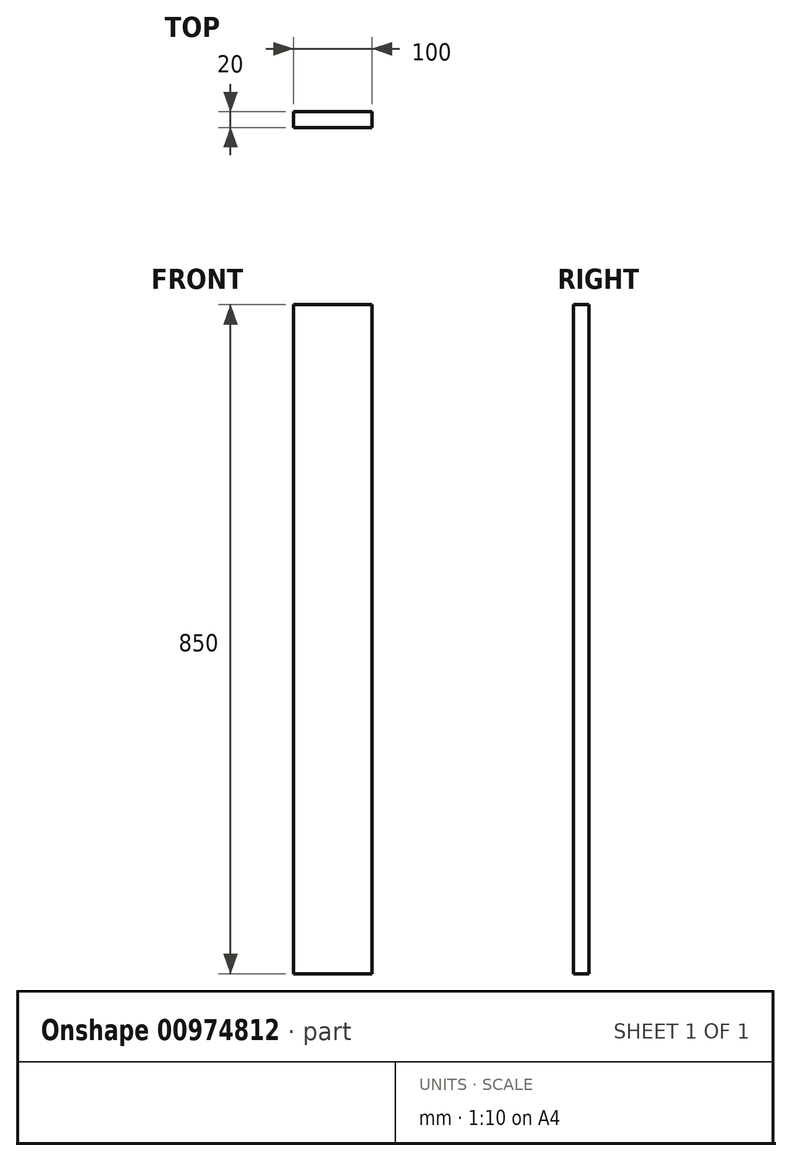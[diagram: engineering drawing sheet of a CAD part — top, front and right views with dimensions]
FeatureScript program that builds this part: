
annotation { "Feature Type Name" : "Feature", "Feature Type Description" : "" }
export const myFeature = defineFeature(function(context is Context, id is Id, definition is map)
    precondition{}
    {
        {
            var Q0;
            Q0=qCreatedBy(makeId("Top.planeOp"),FACE);
            var sketch = newSketch(context, id + "F0", { "sketchPlane" : qUnion([Q0])});
            skLineSegment(sketch, "E0.bottom", {"start": v(50, -10) * mm, "end": v(-50, -10) * mm});
            skLineSegment(sketch, "E0.top", {"start": v(50, 10) * mm, "end": v(-50, 10) * mm});
            skLineSegment(sketch, "E0.left", {"start": v(50, -10) * mm, "end": v(50, 10) * mm});
            skLineSegment(sketch, "E0.right", {"start": v(-50, -10) * mm, "end": v(-50, 10) * mm});
            skPoint(sketch, "E0.middle", {"position": v(0, 0) * mm});
            skSolve(sketch);
        }
        {
            var Q0;
            Q0 = qSketchRegion(id + "F0", true);
            extrude(context, id + "F1", {"entities" : qUnion([Q0]), "endBound" : BoundingType.SYMMETRIC, "depth" : 850 * mm, "offsetDistance" : 25 * mm});
        }
    });
